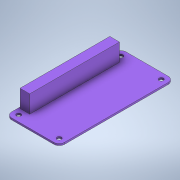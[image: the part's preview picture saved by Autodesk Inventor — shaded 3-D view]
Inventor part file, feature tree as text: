
AUTODESK INVENTOR PART (.ipt)
format: ipt  version: 2021 (Build 250183000, 183)  size: 140,800 bytes
history: native  units: mm
features: extrude x2, sketch x2, fillet x1
ambient origin geometry x8: Origin, YZ Plane, XZ Plane, XY Plane, X Axis, Y Axis, Z Axis, Center Point
bodies: Solid1 (feature_tree)
feature tree (5):
  extrude  "Extrusion1"  Depth=65.0mm
  fillet  "Fillet1"  Radius=23.0mm
  extrude  "Extrusion2"  Depth=3.0mm
  sketch  "Sketch1"  dims[d0=30.0mm d1=65.0mm d2=23.0mm]
  sketch  "Sketch2"  dims[d3=58.0mm d4=2.5mm d5=2.5mm d6=2.5mm d7=2.5mm d8=1.0mm d9=0.0mm d10=3.0mm d11=5.5mm d12=51.0mm d13=3.5mm d14=10.0mm d15=0.0mm d16=3.0mm d17=0.0mm]
